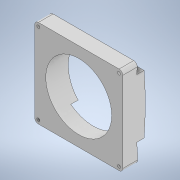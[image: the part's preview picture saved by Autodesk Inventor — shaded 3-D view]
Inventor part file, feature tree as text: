
AUTODESK INVENTOR PART (.ipt)
format: ipt  version: 2022.1 (Build 261234020, 234B)  size: 164,864 bytes
history: native  units: in
note: dims shown in document units (in); Inventor stores cm internally (conversion verified against a paired STEP export)
features: extrude x2, sketch x1, hole x1, fillet x1
ambient origin geometry x8: Origin, YZ Plane, XZ Plane, XY Plane, X Axis, Y Axis, Z Axis, Center Point
bodies: Solid1 (feature_tree)
feature tree (5):
  extrude  "Extrusion1"  Depth=0.25in
  sketch  "Sketch3"  dims[d0=0.5in d1=4.0in d3=2.0in d4=0.0835in d5=24.0in d6=4.0in d7=24.0in d8=0.5in d9=4.0in d10=24.0in d11=6.0in d12=1.001in d13=6.0in d14=0.0in d15=4.5in d16=0.25in d17=0.25in d18=0.0in d19=0.0in d20=0.201in d21=0.75in d22=0.563in d23=0.12in d24=0.5635in d25=1.0in d26=0.8108in d27=0.25in]
  extrude  "Extrusion2"  Depth=0.25in
  hole  "Hole1"  [1 undecoded]
  fillet  "Fillet1"  Radius=24.0in
note: 1 required parameter value undecoded (feature->parameter linkage not recoverable at this tier; creation-order binding heuristic only, values carry confidence <= 0.55)
